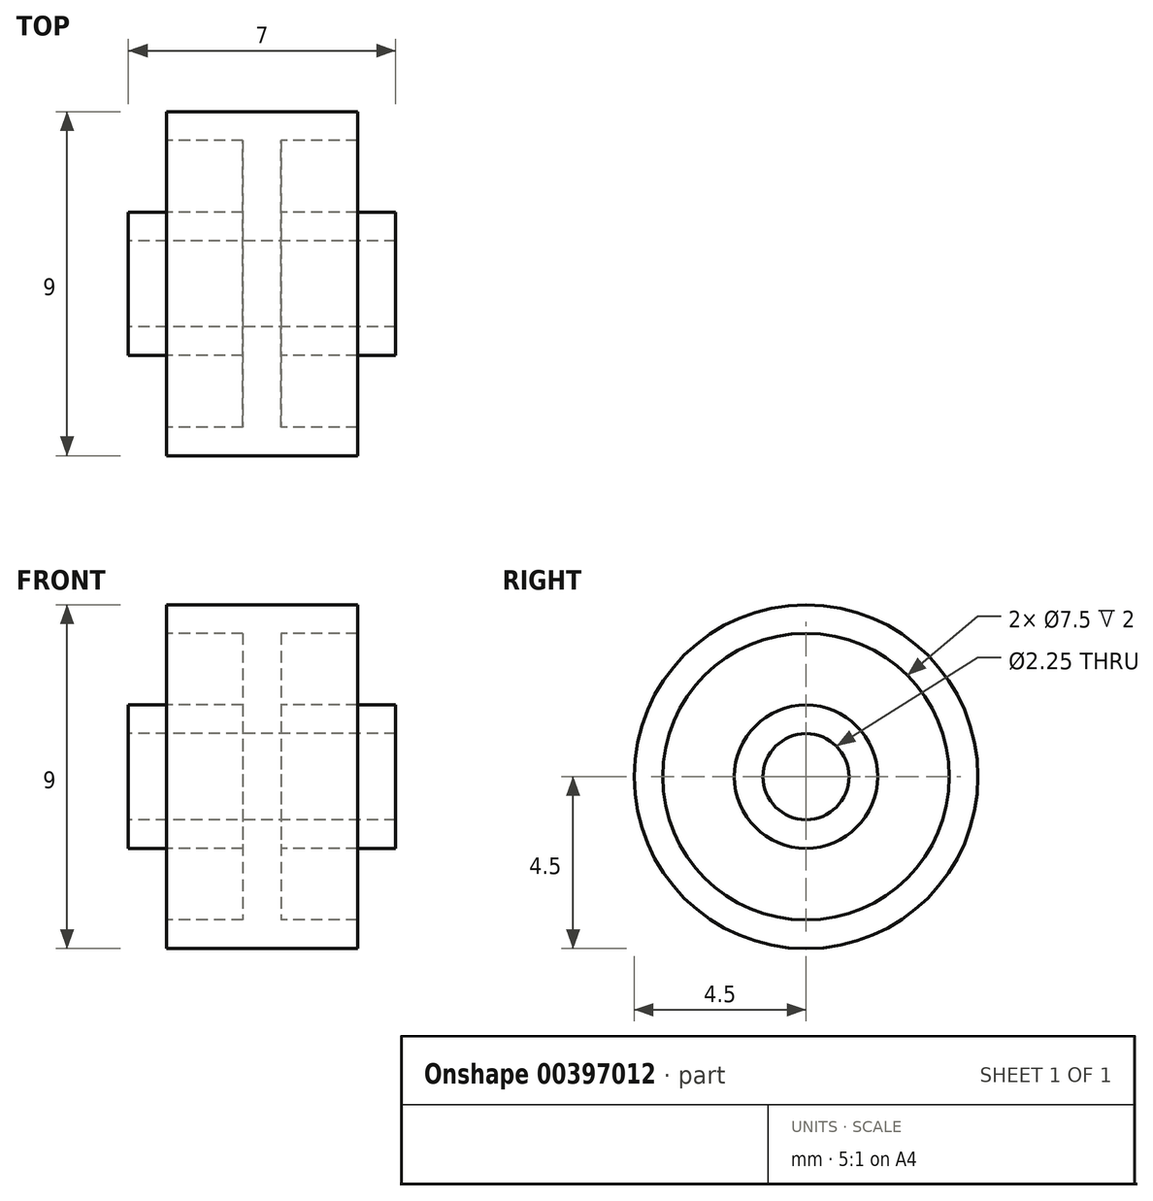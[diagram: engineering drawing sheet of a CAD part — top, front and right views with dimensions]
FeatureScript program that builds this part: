
annotation { "Feature Type Name" : "Feature", "Feature Type Description" : "" }
export const myFeature = defineFeature(function(context is Context, id is Id, definition is map)
    precondition{}
    {
        {
            var Q0;
            Q0=qCreatedBy(makeId("Front.planeOp"),FACE);
            var sketch = newSketch(context, id + "F0", { "sketchPlane" : qUnion([Q0])});
            skLineSegment(sketch, "E0", {"start": v(-10.07, 0) * mm, "end": v(11.96, 0) * mm, "construction": true});
            skLineSegment(sketch, "E1", {"start": v(-3.5, 1.13) * mm, "end": v(3.5, 1.13) * mm});
            skLineSegment(sketch, "E2", {"start": v(3.5, 1.13) * mm, "end": v(3.5, 1.88) * mm});
            skLineSegment(sketch, "E3", {"start": v(3.5, 1.88) * mm, "end": v(0.5, 1.88) * mm});
            skLineSegment(sketch, "E4", {"start": v(0.5, 1.88) * mm, "end": v(0.5, 3.75) * mm});
            skLineSegment(sketch, "E5", {"start": v(0.5, 3.75) * mm, "end": v(2.5, 3.75) * mm});
            skLineSegment(sketch, "E6", {"start": v(2.5, 3.75) * mm, "end": v(2.5, 4.5) * mm});
            skLineSegment(sketch, "E7", {"start": v(2.5, 4.5) * mm, "end": v(-2.5, 4.5) * mm});
            skLineSegment(sketch, "E8", {"start": v(-2.5, 4.5) * mm, "end": v(-2.5, 3.75) * mm});
            skLineSegment(sketch, "E9", {"start": v(-2.5, 3.75) * mm, "end": v(-0.5, 3.75) * mm});
            skLineSegment(sketch, "E10", {"start": v(-0.5, 3.75) * mm, "end": v(-0.5, 1.88) * mm});
            skLineSegment(sketch, "E11", {"start": v(-0.5, 1.88) * mm, "end": v(-3.5, 1.88) * mm});
            skLineSegment(sketch, "E12", {"start": v(-3.5, 1.88) * mm, "end": v(-3.5, 1.13) * mm});
            skLineSegment(sketch, "E13", {"start": v(0, 0) * mm, "end": v(0, 9.85) * mm, "construction": true});
            skSolve(sketch);
        }
        {
            var Q0;
            Q0 = qSketchRegion(id + "F0", true);
            var Q1;
            Q1=sQuery(id+"F0.wireOp",EDGE,"E0");
            revolve(context, id + "F1", {"surfaceOperationType" : NewSurfaceOperationType.NEW, "entities" : qUnion([Q0]), "axis" : qUnion([Q1]), "revolveType" : RevolveType.FULL});
        }
    });
